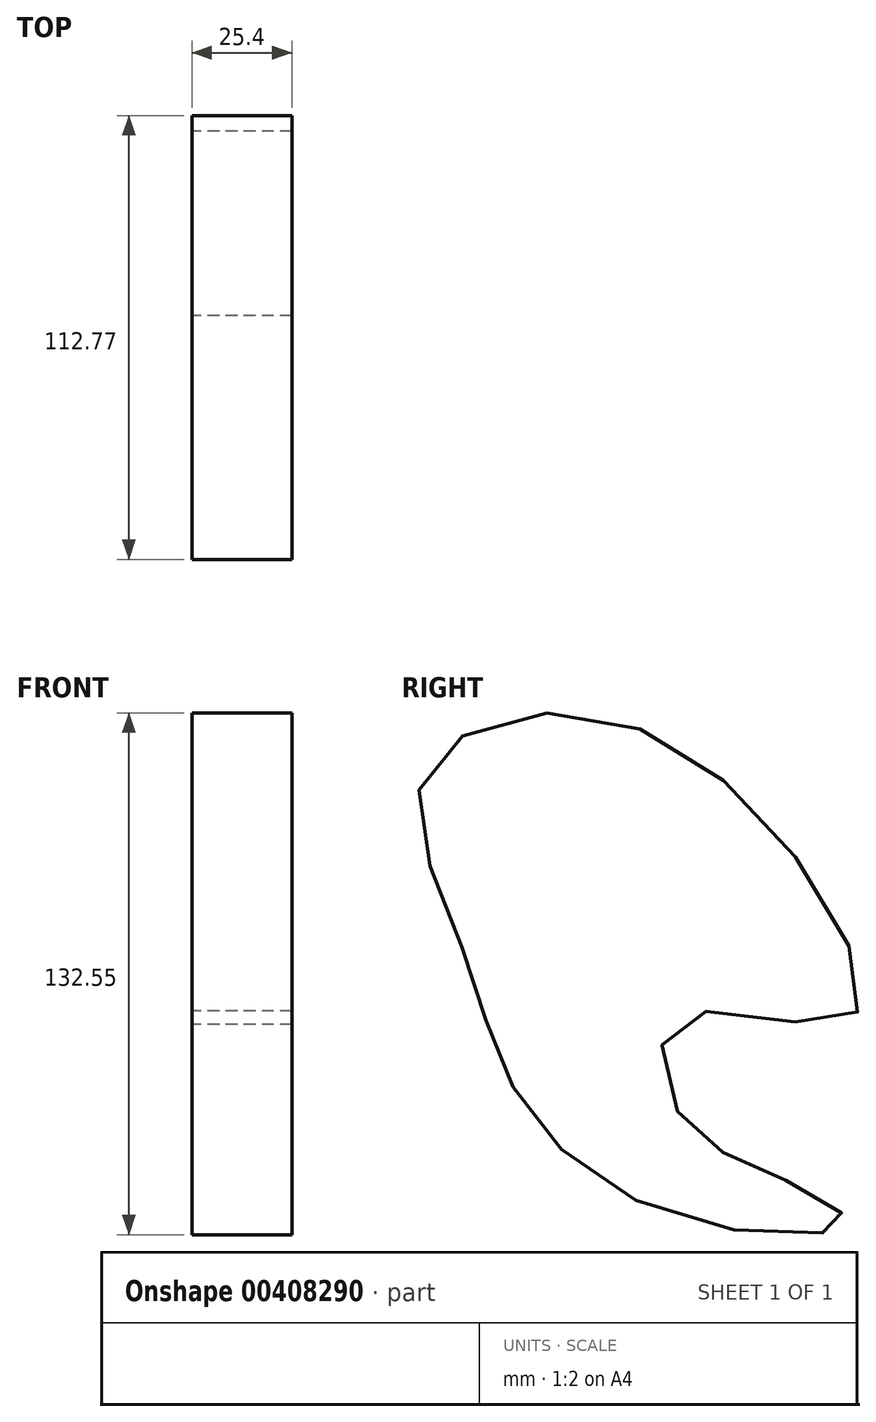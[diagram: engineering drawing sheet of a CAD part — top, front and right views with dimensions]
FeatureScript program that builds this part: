
annotation { "Feature Type Name" : "Feature", "Feature Type Description" : "" }
export const myFeature = defineFeature(function(context is Context, id is Id, definition is map)
    precondition{}
    {
        {
            var Q0;
            Q0=qCreatedBy(makeId("Right.planeOp"),FACE);
            var sketch = newSketch(context, id + "F0", { "sketchPlane" : qUnion([Q0])});
            skFitSpline(sketch, "E0", {"points": [v(-55.2, 29.5) * mm, v(-41.7, -7.04) * mm, v(0, -39.13) * mm, v(42.3, -40.54) * mm, v(24, -28.28) * mm, v(0, -12.93) * mm, v(0, 11.77) * mm, v(43.2, 11.13) * mm, v(31.8, 49.22) * mm, v(-23.7, 88.57) * mm, v(-65.1, 72.9) * mm, v(-55.2, 29.5) * mm]});
            skSolve(sketch);
        }
        {
            var Q0;
            Q0=makeQuery(id+"F0.imprint","IMPRINT",FACE,{"disambiguationData":[TD([[makeQuery(id+"F0.imprint","IMPRINT",EDGE,{"derivedFrom":sQuery(id+"F0.wireOp",EDGE,"E0")}),1.0]])]});
            extrude(context, id + "F1", {"entities" : qUnion([Q0]), "depth" : 25.4 * mm});
        }
    });
